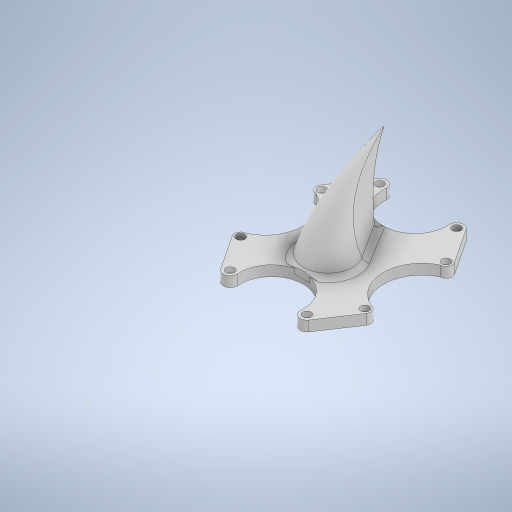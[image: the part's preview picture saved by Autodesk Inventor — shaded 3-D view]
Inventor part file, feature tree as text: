
AUTODESK INVENTOR PART (.ipt)
format: ipt  version: 2023 (Build 270158000, 158)  size: 572,416 bytes
history: native  units: in
note: dims shown in document units (in); Inventor stores cm internally (conversion verified against a paired STEP export)
features: other x3, sketch x3, extrude x2, projected_geometry x2
ambient origin geometry x8: Origin, YZ Plane, XZ Plane, XY Plane, X Axis, Y Axis, Z Axis, Center Point
bodies: Solid2 (feature_tree)
feature tree (10):
  other  "Assembly1.iam"
  other  "Part1.ipt:1"
  other  "Shark fin.ipt:1"
  extrude  "Extrusion1"  Depth=0.3937in
  extrude  "Extrusion2"  Depth=0.1969in
  sketch  "Sketch6"  dims[d5=0.1969in d6=0.1181in d7=0.0in d8=0.1969in d9=0.8465in d10=0.6299in d11=0.0in]
  sketch  "Sketch4"  dims[d1=0.3937in d2=0.1969in]
  projected_geometry  "Projected Loop1"
  sketch  "Sketch5"  dims[d3=0.1969in d4=0.1969in]
  projected_geometry  "Projected Loop2"
